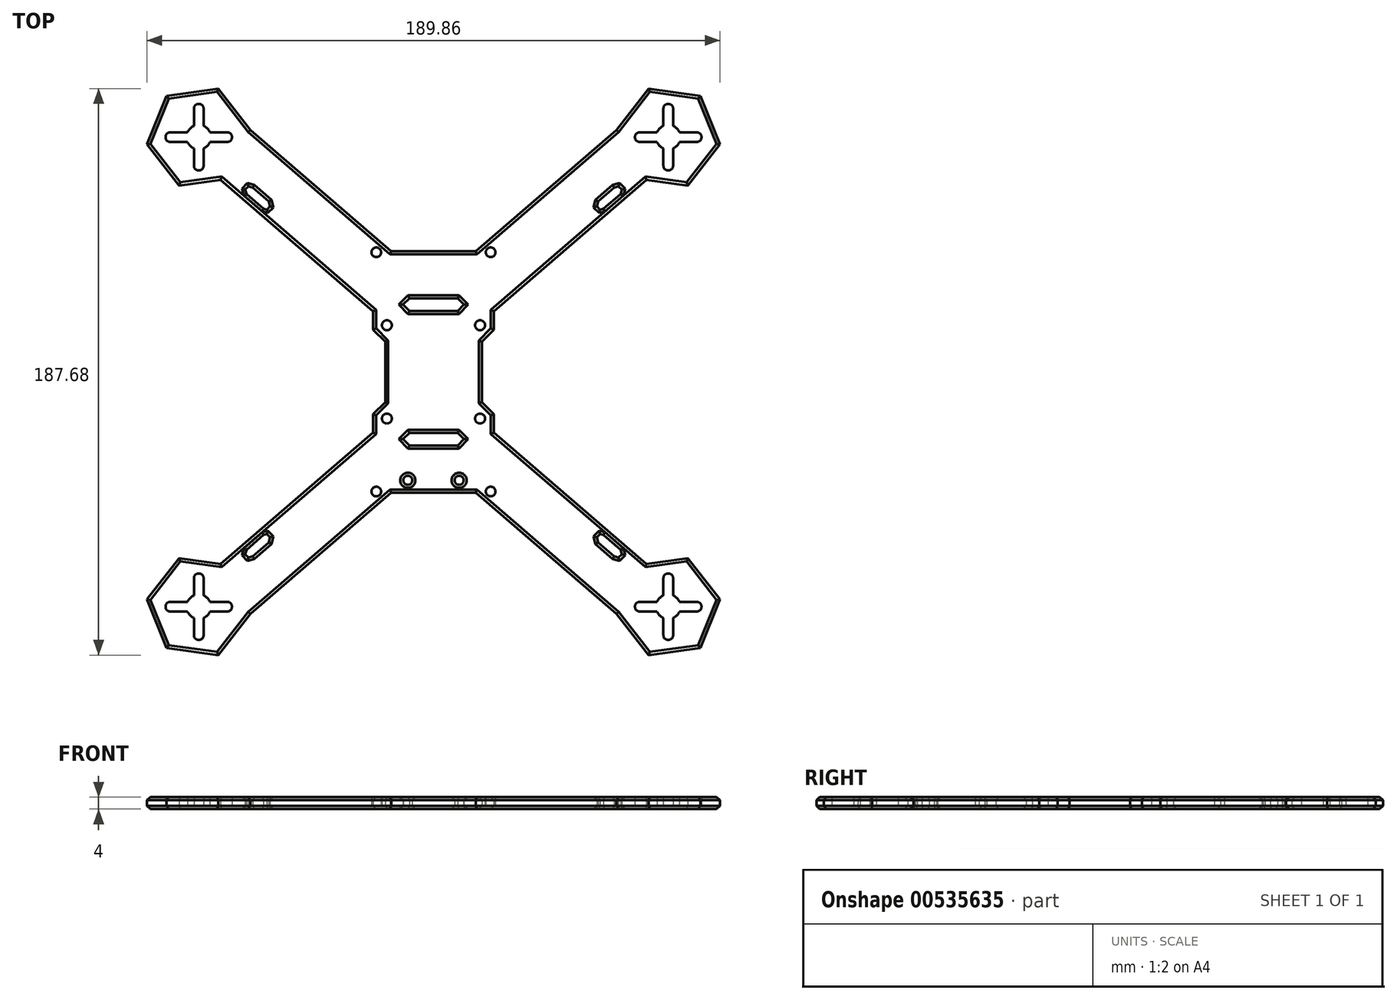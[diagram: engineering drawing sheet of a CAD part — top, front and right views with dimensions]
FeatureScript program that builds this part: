
annotation { "Feature Type Name" : "Feature", "Feature Type Description" : "" }
export const myFeature = defineFeature(function(context is Context, id is Id, definition is map)
    precondition{}
    {
        {
            var Q0;
            Q0=qCreatedBy(makeId("Top.planeOp"),FACE);
            var sketch = newSketch(context, id + "F0", { "sketchPlane" : qUnion([Q0])});
            skCircle(sketch, "E0", {"center": v(15.45, 15.45) * mm, "radius": 1.65 * mm});
            skPoint(sketch, "E1.middle", {"position": v(77.78, 77.78) * mm});
            skLineSegment(sketch, "E2.bottom", {"start": v(77.68, 66.78) * mm, "end": v(77.88, 66.78) * mm});
            skLineSegment(sketch, "E2.top", {"start": v(77.68, 88.78) * mm, "end": v(77.88, 88.78) * mm});
            skLineSegment(sketch, "E2.left", {"start": v(76.18, 68.28) * mm, "end": v(76.18, 76.29) * mm});
            skLineSegment(sketch, "E2.right", {"start": v(79.38, 68.28) * mm, "end": v(79.38, 76.18) * mm});
            skLineSegment(sketch, "E3.bottom", {"start": v(87.28, 79.38) * mm, "end": v(79.38, 79.38) * mm});
            skLineSegment(sketch, "E3.top", {"start": v(87.28, 76.18) * mm, "end": v(79.38, 76.18) * mm});
            skLineSegment(sketch, "E3.left", {"start": v(88.78, 77.88) * mm, "end": v(88.78, 77.68) * mm});
            skLineSegment(sketch, "E3.right", {"start": v(66.78, 77.88) * mm, "end": v(66.78, 77.68) * mm});
            skPoint(sketch, "E4.visualSharp", {"position": v(79.38, 88.78) * mm});
            skArc(sketch, "E4.filletArc", {"start": v(79.38, 87.28) * mm, "mid": v(78.94, 88.34) * mm, "end": v(77.88, 88.78) * mm});
            skPoint(sketch, "E5.visualSharp", {"position": v(76.18, 88.78) * mm});
            skArc(sketch, "E5.filletArc", {"start": v(77.68, 88.78) * mm, "mid": v(76.62, 88.34) * mm, "end": v(76.18, 87.28) * mm});
            skPoint(sketch, "E6.visualSharp", {"position": v(79.38, 66.78) * mm});
            skArc(sketch, "E6.filletArc", {"start": v(77.88, 66.78) * mm, "mid": v(78.94, 67.22) * mm, "end": v(79.38, 68.28) * mm});
            skPoint(sketch, "E7.visualSharp", {"position": v(76.18, 66.78) * mm});
            skArc(sketch, "E7.filletArc", {"start": v(76.18, 68.28) * mm, "mid": v(76.62, 67.22) * mm, "end": v(77.68, 66.78) * mm});
            skPoint(sketch, "E8.visualSharp", {"position": v(88.78, 79.38) * mm});
            skArc(sketch, "E8.filletArc", {"start": v(88.78, 77.88) * mm, "mid": v(88.34, 78.94) * mm, "end": v(87.28, 79.38) * mm});
            skPoint(sketch, "E9.visualSharp", {"position": v(88.78, 76.18) * mm});
            skArc(sketch, "E9.filletArc", {"start": v(87.28, 76.18) * mm, "mid": v(88.34, 76.62) * mm, "end": v(88.78, 77.68) * mm});
            skPoint(sketch, "E10.visualSharp", {"position": v(66.78, 79.38) * mm});
            skArc(sketch, "E10.filletArc", {"start": v(68.28, 79.38) * mm, "mid": v(67.22, 78.94) * mm, "end": v(66.78, 77.88) * mm});
            skPoint(sketch, "E11.visualSharp", {"position": v(66.78, 76.18) * mm});
            skArc(sketch, "E11.filletArc", {"start": v(66.78, 77.68) * mm, "mid": v(67.22, 76.62) * mm, "end": v(68.28, 76.18) * mm});
            skLineSegment(sketch, "E12.trimOffspring", {"start": v(76.18, 79.38) * mm, "end": v(76.18, 87.28) * mm});
            skLineSegment(sketch, "E13.trimOffspring", {"start": v(76.18, 76.18) * mm, "end": v(68.28, 76.18) * mm});
            skLineSegment(sketch, "E14.trimOffspring", {"start": v(76.18, 79.38) * mm, "end": v(68.28, 79.38) * mm});
            skLineSegment(sketch, "E15.trimOffspring", {"start": v(79.38, 79.38) * mm, "end": v(79.38, 87.28) * mm});
            skLineSegment(sketch, "E16.cCircle", {"start": v(49.17, 49.17) * mm, "end": v(49.17, 49.17) * mm});
            skLineSegment(sketch, "E17", {"start": v(77.78, 77.78) * mm, "end": v(0, 0) * mm, "construction": true});
            skLineSegment(sketch, "E18", {"start": v(60.63, 80.19) * mm, "end": v(14, 40) * mm});
            skLineSegment(sketch, "E19", {"start": v(20, 20.09) * mm, "end": v(70.54, 63.65) * mm});
            skLineSegment(sketch, "E20", {"start": v(20, 20.09) * mm, "end": v(20, 14) * mm});
            skLineSegment(sketch, "E21", {"start": v(14, 40) * mm, "end": v(0, 40) * mm});
            skLineSegment(sketch, "E22", {"start": v(61.99, 58.96) * mm, "end": v(56.29, 54.05) * mm});
            skCircle(sketch, "E23", {"center": v(77.78, 77.78) * mm, "radius": 63.5 * mm, "construction": true});
            skLineSegment(sketch, "E24", {"start": v(8, 20.17) * mm, "end": v(0, 20.17) * mm});
            skLineSegment(sketch, "E25", {"start": v(8, 20.17) * mm, "end": v(10.12, 22.3) * mm});
            skLineSegment(sketch, "E26", {"start": v(10.12, 22.3) * mm, "end": v(8, 24.41) * mm});
            skLineSegment(sketch, "E27", {"start": v(8, 24.41) * mm, "end": v(0, 24.41) * mm});
            skLineSegment(sketch, "E28", {"start": v(14, 40) * mm, "end": v(14, 0) * mm, "construction": true});
            skCircle(sketch, "E29", {"center": v(18.94, 39.63) * mm, "radius": 1.6 * mm});
            skLineSegment(sketch, "E30.3", {"start": v(59.86, 61.08) * mm, "end": v(61.31, 61.47) * mm});
            skLineSegment(sketch, "E30.4", {"start": v(61.31, 61.47) * mm, "end": v(62.37, 60.41) * mm});
            skLineSegment(sketch, "E30.5", {"start": v(62.37, 60.41) * mm, "end": v(61.99, 58.96) * mm});
            skLineSegment(sketch, "E31.0", {"start": v(56.29, 54.05) * mm, "end": v(55.18, 53.75) * mm});
            skLineSegment(sketch, "E31.1", {"start": v(55.18, 53.75) * mm, "end": v(54.12, 54.81) * mm});
            skLineSegment(sketch, "E31.2", {"start": v(54.12, 54.81) * mm, "end": v(54.56, 56.5) * mm});
            skLineSegment(sketch, "E32", {"start": v(14, 40) * mm, "end": v(21.57, 46.53) * mm, "construction": true});
            skLineSegment(sketch, "E33", {"start": v(21.57, 46.53) * mm, "end": v(26.14, 41.23) * mm, "construction": true});
            skLineSegment(sketch, "E34", {"start": v(26.14, 41.23) * mm, "end": v(18.57, 34.7) * mm, "construction": true});
            skLineSegment(sketch, "E35", {"start": v(18.57, 34.7) * mm, "end": v(14, 40) * mm, "construction": true});
            skLineSegment(sketch, "E36", {"start": v(59.86, 61.08) * mm, "end": v(54.56, 56.5) * mm});
            skArc(sketch, "E37.MirrorCS", {"start": v(-79.38, 87.28) * mm, "mid": v(-78.94, 88.34) * mm, "end": v(-77.88, 88.78) * mm});
            skArc(sketch, "E38.MirrorCS", {"start": v(-77.68, 88.78) * mm, "mid": v(-76.62, 88.34) * mm, "end": v(-76.18, 87.28) * mm});
            skLineSegment(sketch, "E39.MirrorCS", {"start": v(-76.18, 79.38) * mm, "end": v(-76.18, 87.28) * mm});
            skLineSegment(sketch, "E40.MirrorCS", {"start": v(-76.18, 68.28) * mm, "end": v(-76.18, 76.29) * mm});
            skLineSegment(sketch, "E41.MirrorCS", {"start": v(-79.38, 68.28) * mm, "end": v(-79.38, 76.18) * mm});
            skLineSegment(sketch, "E42.MirrorCS", {"start": v(-87.28, 79.38) * mm, "end": v(-79.38, 79.38) * mm});
            skLineSegment(sketch, "E43.MirrorCS", {"start": v(-87.28, 76.18) * mm, "end": v(-79.38, 76.18) * mm});
            skArc(sketch, "E44.MirrorCS", {"start": v(-77.88, 66.78) * mm, "mid": v(-78.94, 67.22) * mm, "end": v(-79.38, 68.28) * mm});
            skArc(sketch, "E45.MirrorCS", {"start": v(-76.18, 68.28) * mm, "mid": v(-76.62, 67.22) * mm, "end": v(-77.68, 66.78) * mm});
            skArc(sketch, "E46.MirrorCS", {"start": v(-88.78, 77.88) * mm, "mid": v(-88.34, 78.94) * mm, "end": v(-87.28, 79.38) * mm});
            skArc(sketch, "E47.MirrorCS", {"start": v(-87.28, 76.18) * mm, "mid": v(-88.34, 76.62) * mm, "end": v(-88.78, 77.68) * mm});
            skArc(sketch, "E48.MirrorCS", {"start": v(-68.28, 79.38) * mm, "mid": v(-67.22, 78.94) * mm, "end": v(-66.78, 77.88) * mm});
            skArc(sketch, "E49.MirrorCS", {"start": v(-66.78, 77.68) * mm, "mid": v(-67.22, 76.62) * mm, "end": v(-68.28, 76.18) * mm});
            skLineSegment(sketch, "E50.MirrorCS", {"start": v(-79.38, 79.38) * mm, "end": v(-79.38, 87.28) * mm});
            skLineSegment(sketch, "E51.MirrorCS", {"start": v(-10.12, 22.3) * mm, "end": v(-8, 24.41) * mm});
            skPoint(sketch, "E52.MirrorP", {"position": v(-77.78, 77.78) * mm});
            skLineSegment(sketch, "E53.MirrorCS", {"start": v(-8, 20.17) * mm, "end": v(-10.12, 22.3) * mm});
            skLineSegment(sketch, "E54.MirrorCS", {"start": v(-55.18, 53.75) * mm, "end": v(-54.12, 54.81) * mm});
            skLineSegment(sketch, "E55.MirrorCS", {"start": v(-54.12, 54.81) * mm, "end": v(-54.56, 56.5) * mm});
            skLineSegment(sketch, "E56.MirrorCS", {"start": v(-76.18, 76.18) * mm, "end": v(-68.28, 76.18) * mm});
            skLineSegment(sketch, "E57.MirrorCS", {"start": v(-76.18, 79.38) * mm, "end": v(-68.28, 79.38) * mm});
            skCircle(sketch, "E58.MirrorC", {"center": v(-15.45, 15.45) * mm, "radius": 1.65 * mm});
            skLineSegment(sketch, "E59.MirrorCS", {"start": v(-18.57, 34.7) * mm, "end": v(-14, 40) * mm, "construction": true});
            skCircle(sketch, "E60.MirrorC", {"center": v(-18.94, 39.63) * mm, "radius": 1.6 * mm});
            skLineSegment(sketch, "E61.MirrorCS", {"start": v(-62.37, 60.41) * mm, "end": v(-61.99, 58.96) * mm});
            skLineSegment(sketch, "E62.MirrorCS", {"start": v(-59.86, 61.08) * mm, "end": v(-54.56, 56.5) * mm});
            skLineSegment(sketch, "E63.MirrorCS", {"start": v(-59.86, 61.08) * mm, "end": v(-61.31, 61.47) * mm});
            skLineSegment(sketch, "E64.MirrorCS", {"start": v(-21.57, 46.53) * mm, "end": v(-26.14, 41.23) * mm, "construction": true});
            skLineSegment(sketch, "E65.MirrorCS", {"start": v(-56.29, 54.05) * mm, "end": v(-55.18, 53.75) * mm});
            skLineSegment(sketch, "E66.MirrorCS", {"start": v(-61.99, 58.96) * mm, "end": v(-56.29, 54.05) * mm});
            skLineSegment(sketch, "E67.MirrorCS", {"start": v(-61.31, 61.47) * mm, "end": v(-62.37, 60.41) * mm});
            skLineSegment(sketch, "E68.MirrorCS", {"start": v(-8, 24.41) * mm, "end": v(0, 24.41) * mm});
            skLineSegment(sketch, "E69.MirrorCS", {"start": v(-14, 40) * mm, "end": v(-21.57, 46.53) * mm, "construction": true});
            skLineSegment(sketch, "E70.MirrorCS", {"start": v(-20, 20.09) * mm, "end": v(-70.54, 63.65) * mm});
            skPoint(sketch, "E71.MirrorP", {"position": v(-79.38, 88.78) * mm});
            skPoint(sketch, "E72.MirrorP", {"position": v(-88.78, 76.18) * mm});
            skCircle(sketch, "E73.MirrorC", {"center": v(-77.78, 77.78) * mm, "radius": 63.5 * mm, "construction": true});
            skPoint(sketch, "E74.MirrorP", {"position": v(-76.18, 66.78) * mm});
            skPoint(sketch, "E75.MirrorP", {"position": v(-79.38, 66.78) * mm});
            skLineSegment(sketch, "E76.MirrorCS", {"start": v(-14, 40) * mm, "end": v(-14, 0) * mm, "construction": true});
            skLineSegment(sketch, "E77.MirrorCS", {"start": v(-8, 20.17) * mm, "end": v(0, 20.17) * mm});
            skLineSegment(sketch, "E78.MirrorCS", {"start": v(-14, 40) * mm, "end": v(0, 40) * mm});
            skPoint(sketch, "E79.MirrorP", {"position": v(-76.18, 88.78) * mm});
            skLineSegment(sketch, "E80.MirrorCS", {"start": v(-26.14, 41.23) * mm, "end": v(-18.57, 34.7) * mm, "construction": true});
            skLineSegment(sketch, "E81.MirrorCS", {"start": v(-77.78, 77.78) * mm, "end": v(0, 0) * mm, "construction": true});
            skPoint(sketch, "E82.MirrorP", {"position": v(-66.78, 76.18) * mm});
            skPoint(sketch, "E83.MirrorP", {"position": v(-66.78, 79.38) * mm});
            skPoint(sketch, "E84.MirrorP", {"position": v(-88.78, 79.38) * mm});
            skLineSegment(sketch, "E85.MirrorCS", {"start": v(-60.63, 80.19) * mm, "end": v(-14, 40) * mm});
            skArc(sketch, "E86.MirrorCS", {"start": v(76.18, -68.28) * mm, "mid": v(76.62, -67.22) * mm, "end": v(77.68, -66.78) * mm});
            skArc(sketch, "E87.MirrorCS", {"start": v(77.88, -66.78) * mm, "mid": v(78.94, -67.22) * mm, "end": v(79.38, -68.28) * mm});
            skArc(sketch, "E88.MirrorCS", {"start": v(77.68, -88.78) * mm, "mid": v(76.62, -88.34) * mm, "end": v(76.18, -87.28) * mm});
            skArc(sketch, "E89.MirrorCS", {"start": v(79.38, -87.28) * mm, "mid": v(78.94, -88.34) * mm, "end": v(77.88, -88.78) * mm});
            skLineSegment(sketch, "E90.MirrorCS", {"start": v(76.18, -79.38) * mm, "end": v(76.18, -87.28) * mm});
            skLineSegment(sketch, "E91.MirrorCS", {"start": v(-76.18, -79.38) * mm, "end": v(-76.18, -87.28) * mm});
            skArc(sketch, "E92.MirrorCS", {"start": v(-77.68, -88.78) * mm, "mid": v(-76.62, -88.34) * mm, "end": v(-76.18, -87.28) * mm});
            skLineSegment(sketch, "E93.MirrorCS", {"start": v(79.38, -79.38) * mm, "end": v(79.38, -87.28) * mm});
            skArc(sketch, "E94.MirrorCS", {"start": v(66.78, -77.68) * mm, "mid": v(67.22, -76.62) * mm, "end": v(68.28, -76.18) * mm});
            skArc(sketch, "E95.MirrorCS", {"start": v(68.28, -79.38) * mm, "mid": v(67.22, -78.94) * mm, "end": v(66.78, -77.88) * mm});
            skArc(sketch, "E96.MirrorCS", {"start": v(87.28, -76.18) * mm, "mid": v(88.34, -76.62) * mm, "end": v(88.78, -77.68) * mm});
            skArc(sketch, "E97.MirrorCS", {"start": v(88.78, -77.88) * mm, "mid": v(88.34, -78.94) * mm, "end": v(87.28, -79.38) * mm});
            skLineSegment(sketch, "E98.MirrorCS", {"start": v(87.28, -76.18) * mm, "end": v(79.38, -76.18) * mm});
            skLineSegment(sketch, "E99.MirrorCS", {"start": v(79.38, -68.28) * mm, "end": v(79.38, -76.18) * mm});
            skLineSegment(sketch, "E100.MirrorCS", {"start": v(76.18, -68.28) * mm, "end": v(76.18, -76.29) * mm});
            skLineSegment(sketch, "E101.MirrorCS", {"start": v(76.18, -79.38) * mm, "end": v(68.28, -79.38) * mm});
            skLineSegment(sketch, "E102.MirrorCS", {"start": v(76.18, -76.18) * mm, "end": v(68.28, -76.18) * mm});
            skArc(sketch, "E103.MirrorCS", {"start": v(-79.38, -87.28) * mm, "mid": v(-78.94, -88.34) * mm, "end": v(-77.88, -88.78) * mm});
            skLineSegment(sketch, "E104.MirrorCS", {"start": v(-79.38, -79.38) * mm, "end": v(-79.38, -87.28) * mm});
            skArc(sketch, "E105.MirrorCS", {"start": v(-87.28, -76.18) * mm, "mid": v(-88.34, -76.62) * mm, "end": v(-88.78, -77.68) * mm});
            skArc(sketch, "E106.MirrorCS", {"start": v(-88.78, -77.88) * mm, "mid": v(-88.34, -78.94) * mm, "end": v(-87.28, -79.38) * mm});
            skArc(sketch, "E107.MirrorCS", {"start": v(-76.18, -68.28) * mm, "mid": v(-76.62, -67.22) * mm, "end": v(-77.68, -66.78) * mm});
            skLineSegment(sketch, "E108.MirrorCS", {"start": v(87.28, -79.38) * mm, "end": v(79.38, -79.38) * mm});
            skArc(sketch, "E109.MirrorCS", {"start": v(-77.88, -66.78) * mm, "mid": v(-78.94, -67.22) * mm, "end": v(-79.38, -68.28) * mm});
            skLineSegment(sketch, "E110.MirrorCS", {"start": v(-87.28, -79.38) * mm, "end": v(-79.38, -79.38) * mm});
            skArc(sketch, "E111.MirrorCS", {"start": v(-66.78, -77.68) * mm, "mid": v(-67.22, -76.62) * mm, "end": v(-68.28, -76.18) * mm});
            skPoint(sketch, "E112.MirrorP", {"position": v(77.78, -77.78) * mm});
            skLineSegment(sketch, "E113.MirrorCS", {"start": v(-87.28, -76.18) * mm, "end": v(-79.38, -76.18) * mm});
            skLineSegment(sketch, "E114.MirrorCS", {"start": v(54.12, -54.81) * mm, "end": v(54.56, -56.5) * mm});
            skArc(sketch, "E115.MirrorCS", {"start": v(-68.28, -79.38) * mm, "mid": v(-67.22, -78.94) * mm, "end": v(-66.78, -77.88) * mm});
            skLineSegment(sketch, "E116.MirrorCS", {"start": v(55.18, -53.75) * mm, "end": v(54.12, -54.81) * mm});
            skLineSegment(sketch, "E117.MirrorCS", {"start": v(-76.18, -68.28) * mm, "end": v(-76.18, -76.29) * mm});
            skLineSegment(sketch, "E118.MirrorCS", {"start": v(-59.86, -61.08) * mm, "end": v(-61.31, -61.47) * mm});
            skLineSegment(sketch, "E119.MirrorCS", {"start": v(8, -20.17) * mm, "end": v(10.12, -22.3) * mm});
            skLineSegment(sketch, "E120.MirrorCS", {"start": v(56.29, -54.05) * mm, "end": v(55.18, -53.75) * mm});
            skLineSegment(sketch, "E121.MirrorCS", {"start": v(59.86, -61.08) * mm, "end": v(54.56, -56.5) * mm});
            skLineSegment(sketch, "E122.MirrorCS", {"start": v(62.37, -60.41) * mm, "end": v(61.99, -58.96) * mm});
            skLineSegment(sketch, "E123.MirrorCS", {"start": v(-54.12, -54.81) * mm, "end": v(-54.56, -56.5) * mm});
            skLineSegment(sketch, "E124.MirrorCS", {"start": v(-59.86, -61.08) * mm, "end": v(-54.56, -56.5) * mm});
            skLineSegment(sketch, "E125.MirrorCS", {"start": v(18.57, -34.7) * mm, "end": v(14, -40) * mm, "construction": true});
            skCircle(sketch, "E126.MirrorC", {"center": v(15.45, -15.45) * mm, "radius": 1.65 * mm});
            skLineSegment(sketch, "E127.MirrorCS", {"start": v(61.31, -61.47) * mm, "end": v(62.37, -60.41) * mm});
            skLineSegment(sketch, "E128.MirrorCS", {"start": v(-62.37, -60.41) * mm, "end": v(-61.99, -58.96) * mm});
            skLineSegment(sketch, "E129.MirrorCS", {"start": v(-55.18, -53.75) * mm, "end": v(-54.12, -54.81) * mm});
            skLineSegment(sketch, "E130.MirrorCS", {"start": v(61.99, -58.96) * mm, "end": v(56.29, -54.05) * mm});
            skLineSegment(sketch, "E131.MirrorCS", {"start": v(-10.12, -22.3) * mm, "end": v(-8, -24.41) * mm});
            skLineSegment(sketch, "E132.MirrorCS", {"start": v(-18.57, -34.7) * mm, "end": v(-14, -40) * mm, "construction": true});
            skLineSegment(sketch, "E133.MirrorCS", {"start": v(-61.31, -61.47) * mm, "end": v(-62.37, -60.41) * mm});
            skLineSegment(sketch, "E134.MirrorCS", {"start": v(-56.29, -54.05) * mm, "end": v(-55.18, -53.75) * mm});
            skLineSegment(sketch, "E135.MirrorCS", {"start": v(21.57, -46.53) * mm, "end": v(26.14, -41.23) * mm, "construction": true});
            skLineSegment(sketch, "E136.MirrorCS", {"start": v(59.86, -61.08) * mm, "end": v(61.31, -61.47) * mm});
            skLineSegment(sketch, "E137.MirrorCS", {"start": v(-8, -20.17) * mm, "end": v(-10.12, -22.3) * mm});
            skLineSegment(sketch, "E138.MirrorCS", {"start": v(-61.99, -58.96) * mm, "end": v(-56.29, -54.05) * mm});
            skLineSegment(sketch, "E139.MirrorCS", {"start": v(-79.38, -68.28) * mm, "end": v(-79.38, -76.18) * mm});
            skLineSegment(sketch, "E140.MirrorCS", {"start": v(-21.57, -46.53) * mm, "end": v(-26.14, -41.23) * mm, "construction": true});
            skLineSegment(sketch, "E141.MirrorCS", {"start": v(10.12, -22.3) * mm, "end": v(8, -24.41) * mm});
            skPoint(sketch, "E142.MirrorP", {"position": v(-77.78, -77.78) * mm});
            skLineSegment(sketch, "E143.MirrorCS", {"start": v(26.14, -41.23) * mm, "end": v(18.57, -34.7) * mm, "construction": true});
            skCircle(sketch, "E144.MirrorC", {"center": v(18.94, -39.63) * mm, "radius": 1.6 * mm});
            skLineSegment(sketch, "E145.MirrorCS", {"start": v(14, -40) * mm, "end": v(21.57, -46.53) * mm, "construction": true});
            skLineSegment(sketch, "E146.MirrorCS", {"start": v(8, -24.41) * mm, "end": v(0, -24.41) * mm});
            skCircle(sketch, "E147.MirrorC", {"center": v(-18.94, -39.63) * mm, "radius": 1.6 * mm});
            skLineSegment(sketch, "E148.MirrorCS", {"start": v(14, -40) * mm, "end": v(0, -40) * mm});
            skCircle(sketch, "E149.MirrorC", {"center": v(-15.45, -15.45) * mm, "radius": 1.65 * mm});
            skLineSegment(sketch, "E150.MirrorCS", {"start": v(-26.14, -41.23) * mm, "end": v(-18.57, -34.7) * mm, "construction": true});
            skPoint(sketch, "E151.MirrorP", {"position": v(-76.18, -88.78) * mm});
            skLineSegment(sketch, "E152.MirrorCS", {"start": v(-76.18, -79.38) * mm, "end": v(-68.28, -79.38) * mm});
            skLineSegment(sketch, "E153.MirrorCS", {"start": v(-20, -20.09) * mm, "end": v(-70.54, -63.65) * mm});
            skLineSegment(sketch, "E154.MirrorCS", {"start": v(60.63, -80.19) * mm, "end": v(14, -40) * mm});
            skLineSegment(sketch, "E155.MirrorCS", {"start": v(-14, -40) * mm, "end": v(0, -40) * mm});
            skPoint(sketch, "E156.MirrorP", {"position": v(76.18, -88.78) * mm});
            skLineSegment(sketch, "E157.MirrorCS", {"start": v(-76.18, -76.18) * mm, "end": v(-68.28, -76.18) * mm});
            skLineSegment(sketch, "E158.MirrorCS", {"start": v(77.78, -77.78) * mm, "end": v(0, 0) * mm, "construction": true});
            skLineSegment(sketch, "E159.MirrorCS", {"start": v(-8, -20.17) * mm, "end": v(0, -20.17) * mm});
            skLineSegment(sketch, "E160.MirrorCS", {"start": v(8, -20.17) * mm, "end": v(0, -20.17) * mm});
            skPoint(sketch, "E161.MirrorP", {"position": v(88.78, -79.38) * mm});
            skPoint(sketch, "E162.MirrorP", {"position": v(-79.38, -66.78) * mm});
            skLineSegment(sketch, "E163.MirrorCS", {"start": v(-14, -40) * mm, "end": v(-21.57, -46.53) * mm, "construction": true});
            skPoint(sketch, "E164.MirrorP", {"position": v(79.38, -88.78) * mm});
            skLineSegment(sketch, "E165.MirrorCS", {"start": v(-14, -40) * mm, "end": v(-14, 0) * mm, "construction": true});
            skCircle(sketch, "E166.MirrorC", {"center": v(77.78, -77.78) * mm, "radius": 63.5 * mm, "construction": true});
            skPoint(sketch, "E167.MirrorP", {"position": v(-76.18, -66.78) * mm});
            skLineSegment(sketch, "E168.MirrorCS", {"start": v(-8, -24.41) * mm, "end": v(0, -24.41) * mm});
            skPoint(sketch, "E169.MirrorP", {"position": v(76.18, -66.78) * mm});
            skPoint(sketch, "E170.MirrorP", {"position": v(66.78, -79.38) * mm});
            skPoint(sketch, "E171.MirrorP", {"position": v(-66.78, -79.38) * mm});
            skCircle(sketch, "E172.MirrorC", {"center": v(-77.78, -77.78) * mm, "radius": 63.5 * mm, "construction": true});
            skLineSegment(sketch, "E173.MirrorCS", {"start": v(20, -20.09) * mm, "end": v(20, -14) * mm});
            skLineSegment(sketch, "E174.MirrorCS", {"start": v(14, -40) * mm, "end": v(14, 0) * mm, "construction": true});
            skLineSegment(sketch, "E175.MirrorCS", {"start": v(-77.78, -77.78) * mm, "end": v(0, 0) * mm, "construction": true});
            skPoint(sketch, "E176.MirrorP", {"position": v(-79.38, -88.78) * mm});
            skPoint(sketch, "E177.MirrorP", {"position": v(-88.78, -79.38) * mm});
            skPoint(sketch, "E178.MirrorP", {"position": v(79.38, -66.78) * mm});
            skPoint(sketch, "E179.MirrorP", {"position": v(88.78, -76.18) * mm});
            skPoint(sketch, "E180.MirrorP", {"position": v(-66.78, -76.18) * mm});
            skPoint(sketch, "E181.MirrorP", {"position": v(-88.78, -76.18) * mm});
            skPoint(sketch, "E182.MirrorP", {"position": v(66.78, -76.18) * mm});
            skLineSegment(sketch, "E183.MirrorCS", {"start": v(20, -20.09) * mm, "end": v(70.54, -63.65) * mm});
            skLineSegment(sketch, "E184.MirrorCS", {"start": v(-60.63, -80.19) * mm, "end": v(-14, -40) * mm});
            skCircle(sketch, "E185", {"center": v(8.5, -35.92) * mm, "radius": 1.5 * mm});
            skCircle(sketch, "E186.MirrorC", {"center": v(-8.5, -35.92) * mm, "radius": 1.5 * mm});
            skLineSegment(sketch, "E187", {"start": v(20, -14) * mm, "end": v(16, -10) * mm});
            skLineSegment(sketch, "E188", {"start": v(16, -10) * mm, "end": v(16, 0) * mm});
            skLineSegment(sketch, "E189.MirrorCS", {"start": v(20, 14) * mm, "end": v(16, 10) * mm});
            skLineSegment(sketch, "E190.MirrorCS", {"start": v(16, 10) * mm, "end": v(16, 0) * mm});
            skLineSegment(sketch, "E191.MirrorCS", {"start": v(-20, 20.09) * mm, "end": v(-20, 14) * mm});
            skLineSegment(sketch, "E192.MirrorCS", {"start": v(-16, 10) * mm, "end": v(-16, 0) * mm});
            skLineSegment(sketch, "E193.MirrorCS", {"start": v(-20, -20.09) * mm, "end": v(-20, -14) * mm});
            skLineSegment(sketch, "E194.MirrorCS", {"start": v(-20, -14) * mm, "end": v(-16, -10) * mm});
            skLineSegment(sketch, "E195.MirrorCS", {"start": v(-16, -10) * mm, "end": v(-16, 0) * mm});
            skLineSegment(sketch, "E196.MirrorCS", {"start": v(-20, 14) * mm, "end": v(-16, 10) * mm});
            skLineSegment(sketch, "E197.0", {"start": v(71.29, -93.84) * mm, "end": v(60.63, -80.19) * mm});
            skLineSegment(sketch, "E197.2", {"start": v(70.54, -63.65) * mm, "end": v(84.28, -61.72) * mm});
            skLineSegment(sketch, "E197.3", {"start": v(84.28, -61.72) * mm, "end": v(94.93, -75.38) * mm});
            skLineSegment(sketch, "E197.4", {"start": v(94.93, -75.38) * mm, "end": v(88.44, -91.43) * mm});
            skLineSegment(sketch, "E197.5", {"start": v(88.44, -91.43) * mm, "end": v(71.29, -93.84) * mm});
            skPoint(sketch, "E197.0.midPoint", {"position": v(65.96, -87.01) * mm});
            skLineSegment(sketch, "E198.MirrorCS", {"start": v(-70.54, -63.65) * mm, "end": v(-84.28, -61.72) * mm});
            skLineSegment(sketch, "E199.MirrorCS", {"start": v(-84.28, -61.72) * mm, "end": v(-94.93, -75.38) * mm});
            skLineSegment(sketch, "E200.MirrorCS", {"start": v(-94.93, -75.38) * mm, "end": v(-88.44, -91.43) * mm});
            skLineSegment(sketch, "E201.MirrorCS", {"start": v(-71.29, -93.84) * mm, "end": v(-60.63, -80.19) * mm});
            skLineSegment(sketch, "E202.MirrorCS", {"start": v(-88.44, -91.43) * mm, "end": v(-71.29, -93.84) * mm});
            skLineSegment(sketch, "E203.MirrorCS", {"start": v(-70.54, 63.65) * mm, "end": v(-84.28, 61.72) * mm});
            skLineSegment(sketch, "E204.MirrorCS", {"start": v(-84.28, 61.72) * mm, "end": v(-94.93, 75.38) * mm});
            skLineSegment(sketch, "E205.MirrorCS", {"start": v(-94.93, 75.38) * mm, "end": v(-88.44, 91.43) * mm});
            skLineSegment(sketch, "E206.MirrorCS", {"start": v(-71.29, 93.84) * mm, "end": v(-60.63, 80.19) * mm});
            skLineSegment(sketch, "E207.MirrorCS", {"start": v(-88.44, 91.43) * mm, "end": v(-71.29, 93.84) * mm});
            skLineSegment(sketch, "E208.MirrorCS", {"start": v(70.54, 63.65) * mm, "end": v(84.28, 61.72) * mm});
            skLineSegment(sketch, "E209.MirrorCS", {"start": v(84.28, 61.72) * mm, "end": v(94.93, 75.38) * mm});
            skLineSegment(sketch, "E210.MirrorCS", {"start": v(94.93, 75.38) * mm, "end": v(88.44, 91.43) * mm});
            skLineSegment(sketch, "E211.MirrorCS", {"start": v(71.29, 93.84) * mm, "end": v(60.63, 80.19) * mm});
            skLineSegment(sketch, "E212.MirrorCS", {"start": v(88.44, 91.43) * mm, "end": v(71.29, 93.84) * mm});
            skLineSegment(sketch, "E213", {"start": v(-77.68, -66.78) * mm, "end": v(-77.88, -66.78) * mm});
            skLineSegment(sketch, "E214", {"start": v(-77.68, -88.78) * mm, "end": v(-77.88, -88.78) * mm});
            skLineSegment(sketch, "E215", {"start": v(-88.78, -77.68) * mm, "end": v(-88.78, -77.88) * mm});
            skLineSegment(sketch, "E216", {"start": v(-66.78, -77.68) * mm, "end": v(-66.78, -77.88) * mm});
            skLineSegment(sketch, "E217", {"start": v(-77.68, 88.78) * mm, "end": v(-77.88, 88.78) * mm});
            skLineSegment(sketch, "E218", {"start": v(-66.78, 77.88) * mm, "end": v(-66.78, 77.68) * mm});
            skLineSegment(sketch, "E219", {"start": v(-88.78, 77.88) * mm, "end": v(-88.78, 77.68) * mm});
            skLineSegment(sketch, "E220", {"start": v(-77.88, 66.78) * mm, "end": v(-77.68, 66.78) * mm});
            skLineSegment(sketch, "E221", {"start": v(88.78, -77.68) * mm, "end": v(88.78, -77.88) * mm});
            skLineSegment(sketch, "E222", {"start": v(77.68, -66.78) * mm, "end": v(77.88, -66.78) * mm});
            skLineSegment(sketch, "E223", {"start": v(66.78, -77.68) * mm, "end": v(66.78, -77.88) * mm});
            skLineSegment(sketch, "E224", {"start": v(77.68, -88.78) * mm, "end": v(77.88, -88.78) * mm});
            skCircle(sketch, "E225", {"center": v(77.78, 77.78) * mm, "radius": 4.05 * mm});
            skCircle(sketch, "E226.MirrorC", {"center": v(-77.78, 77.78) * mm, "radius": 4.05 * mm});
            skCircle(sketch, "E227.MirrorC", {"center": v(77.78, -77.78) * mm, "radius": 4.05 * mm});
            skCircle(sketch, "E228.MirrorC", {"center": v(-77.78, -77.78) * mm, "radius": 4.05 * mm});
            skSolve(sketch);
        }
        {
            var Q0;
            Q0=makeQuery(id+"F0.imprint","IMPRINT",FACE,{"disambiguationData":[TD([[makeQuery(id+"F0.imprint","IMPRINT",EDGE,{"derivedFrom":sQuery(id+"F0.wireOp",EDGE,"E0")}),-1.0]])]});
            extrude(context, id + "F1", {"entities" : qUnion([Q0]), "depth" : 4 * mm});
        }
        {
            var Q0;
            Q0=makeQuery(id+"F1.opExtrude","CAP_EDGE",EDGE,{"disambiguationData":[OSD([sQuery(id+"F0.wireOp",EDGE,"E119.MirrorCS")])],"isStart":true});
            var Q1;
            Q1=makeQuery(id+"F1.opExtrude","CAP_EDGE",EDGE,{"disambiguationData":[OSD([sQuery(id+"F0.wireOp",EDGE,"E141.MirrorCS")])],"isStart":true});
            var Q2;
            Q2=makeQuery(id+"F1.opExtrude","CAP_EDGE",EDGE,{"disambiguationData":[OSD([sQuery(id+"F0.wireOp",EDGE,"E159.MirrorCS"),sQuery(id+"F0.wireOp",EDGE,"E160.MirrorCS")])],"isStart":true});
            var Q3;
            Q3=makeQuery(id+"F1.opExtrude","CAP_EDGE",EDGE,{"disambiguationData":[OSD([sQuery(id+"F0.wireOp",EDGE,"E137.MirrorCS")])],"isStart":true});
            var Q4;
            Q4=makeQuery(id+"F1.opExtrude","CAP_EDGE",EDGE,{"disambiguationData":[OSD([sQuery(id+"F0.wireOp",EDGE,"E131.MirrorCS")])],"isStart":true});
            var Q5;
            Q5=makeQuery(id+"F1.opExtrude","CAP_EDGE",EDGE,{"disambiguationData":[OSD([sQuery(id+"F0.wireOp",EDGE,"E146.MirrorCS"),sQuery(id+"F0.wireOp",EDGE,"E168.MirrorCS")])],"isStart":true});
            var Q6;
            Q6=makeQuery(id+"F1.opExtrude","CAP_EDGE",EDGE,{"disambiguationData":[OSD([sQuery(id+"F0.wireOp",EDGE,"E27"),sQuery(id+"F0.wireOp",EDGE,"E68.MirrorCS")])],"isStart":true});
            var Q7;
            Q7=makeQuery(id+"F1.opExtrude","CAP_EDGE",EDGE,{"disambiguationData":[OSD([sQuery(id+"F0.wireOp",EDGE,"E26")])],"isStart":true});
            var Q8;
            Q8=makeQuery(id+"F1.opExtrude","CAP_EDGE",EDGE,{"disambiguationData":[OSD([sQuery(id+"F0.wireOp",EDGE,"E25")])],"isStart":true});
            var Q9;
            Q9=makeQuery(id+"F1.opExtrude","CAP_EDGE",EDGE,{"disambiguationData":[OSD([sQuery(id+"F0.wireOp",EDGE,"E24"),sQuery(id+"F0.wireOp",EDGE,"E77.MirrorCS")])],"isStart":true});
            var Q10;
            Q10=makeQuery(id+"F1.opExtrude","CAP_EDGE",EDGE,{"disambiguationData":[OSD([sQuery(id+"F0.wireOp",EDGE,"E53.MirrorCS")])],"isStart":true});
            var Q11;
            Q11=makeQuery(id+"F1.opExtrude","CAP_EDGE",EDGE,{"disambiguationData":[OSD([sQuery(id+"F0.wireOp",EDGE,"E51.MirrorCS")])],"isStart":true});
            chamfer(context, id + "F2", {"entities" : qUnion([Q0, Q1, Q2, Q3, Q4, Q5, Q6, Q7, Q8, Q9, Q10, Q11]), "width" : 1 * mm, "tangentPropagation" : true});
        }
        {
            var Q0;
            Q0=makeQuery(id+"F1.opExtrude","CAP_EDGE",EDGE,{"disambiguationData":[OSD([sQuery(id+"F0.wireOp",EDGE,"E51.MirrorCS")])],"isStart":false});
            var Q1;
            Q1=makeQuery(id+"F1.opExtrude","CAP_EDGE",EDGE,{"disambiguationData":[OSD([sQuery(id+"F0.wireOp",EDGE,"E53.MirrorCS")])],"isStart":false});
            var Q2;
            Q2=makeQuery(id+"F1.opExtrude","CAP_EDGE",EDGE,{"disambiguationData":[OSD([sQuery(id+"F0.wireOp",EDGE,"E24"),sQuery(id+"F0.wireOp",EDGE,"E77.MirrorCS")])],"isStart":false});
            var Q3;
            Q3=makeQuery(id+"F1.opExtrude","CAP_EDGE",EDGE,{"disambiguationData":[OSD([sQuery(id+"F0.wireOp",EDGE,"E27"),sQuery(id+"F0.wireOp",EDGE,"E68.MirrorCS")])],"isStart":false});
            var Q4;
            Q4=makeQuery(id+"F1.opExtrude","CAP_EDGE",EDGE,{"disambiguationData":[OSD([sQuery(id+"F0.wireOp",EDGE,"E26")])],"isStart":false});
            var Q5;
            Q5=makeQuery(id+"F1.opExtrude","CAP_EDGE",EDGE,{"disambiguationData":[OSD([sQuery(id+"F0.wireOp",EDGE,"E25")])],"isStart":false});
            var Q6;
            Q6=makeQuery(id+"F1.opExtrude","CAP_EDGE",EDGE,{"disambiguationData":[OSD([sQuery(id+"F0.wireOp",EDGE,"E137.MirrorCS")])],"isStart":false});
            var Q7;
            Q7=makeQuery(id+"F1.opExtrude","CAP_EDGE",EDGE,{"disambiguationData":[OSD([sQuery(id+"F0.wireOp",EDGE,"E131.MirrorCS")])],"isStart":false});
            var Q8;
            Q8=makeQuery(id+"F1.opExtrude","CAP_EDGE",EDGE,{"disambiguationData":[OSD([sQuery(id+"F0.wireOp",EDGE,"E159.MirrorCS"),sQuery(id+"F0.wireOp",EDGE,"E160.MirrorCS")])],"isStart":false});
            var Q9;
            Q9=makeQuery(id+"F1.opExtrude","CAP_EDGE",EDGE,{"disambiguationData":[OSD([sQuery(id+"F0.wireOp",EDGE,"E146.MirrorCS"),sQuery(id+"F0.wireOp",EDGE,"E168.MirrorCS")])],"isStart":false});
            var Q10;
            Q10=makeQuery(id+"F1.opExtrude","CAP_EDGE",EDGE,{"disambiguationData":[OSD([sQuery(id+"F0.wireOp",EDGE,"E141.MirrorCS")])],"isStart":false});
            var Q11;
            Q11=makeQuery(id+"F1.opExtrude","CAP_EDGE",EDGE,{"disambiguationData":[OSD([sQuery(id+"F0.wireOp",EDGE,"E119.MirrorCS")])],"isStart":false});
            chamfer(context, id + "F3", {"entities" : qUnion([Q0, Q1, Q2, Q3, Q4, Q5, Q6, Q7, Q8, Q9, Q10, Q11]), "width" : 1 * mm, "tangentPropagation" : true});
        }
        {
            var Q0;
            Q0=makeQuery(id+"F1.opExtrude","CAP_EDGE",EDGE,{"disambiguationData":[OSD([sQuery(id+"F0.wireOp",EDGE,"E36")])],"isStart":false});
            var Q1;
            Q1=makeQuery(id+"F1.opExtrude","CAP_EDGE",EDGE,{"disambiguationData":[OSD([sQuery(id+"F0.wireOp",EDGE,"E30.3")])],"isStart":false});
            var Q2;
            Q2=makeQuery(id+"F1.opExtrude","CAP_EDGE",EDGE,{"disambiguationData":[OSD([sQuery(id+"F0.wireOp",EDGE,"E30.4")])],"isStart":false});
            var Q3;
            Q3=makeQuery(id+"F1.opExtrude","CAP_EDGE",EDGE,{"disambiguationData":[OSD([sQuery(id+"F0.wireOp",EDGE,"E30.5")])],"isStart":false});
            var Q4;
            Q4=makeQuery(id+"F1.opExtrude","CAP_EDGE",EDGE,{"disambiguationData":[OSD([sQuery(id+"F0.wireOp",EDGE,"E22")])],"isStart":false});
            var Q5;
            Q5=makeQuery(id+"F1.opExtrude","CAP_EDGE",EDGE,{"disambiguationData":[OSD([sQuery(id+"F0.wireOp",EDGE,"E31.0")])],"isStart":false});
            var Q6;
            Q6=makeQuery(id+"F1.opExtrude","CAP_EDGE",EDGE,{"disambiguationData":[OSD([sQuery(id+"F0.wireOp",EDGE,"E31.1")])],"isStart":false});
            var Q7;
            Q7=makeQuery(id+"F1.opExtrude","CAP_EDGE",EDGE,{"disambiguationData":[OSD([sQuery(id+"F0.wireOp",EDGE,"E31.2")])],"isStart":false});
            var Q8;
            Q8=makeQuery(id+"F1.opExtrude","CAP_EDGE",EDGE,{"disambiguationData":[OSD([sQuery(id+"F0.wireOp",EDGE,"E22")])],"isStart":true});
            var Q9;
            Q9=makeQuery(id+"F1.opExtrude","CAP_EDGE",EDGE,{"disambiguationData":[OSD([sQuery(id+"F0.wireOp",EDGE,"E31.0")])],"isStart":true});
            var Q10;
            Q10=makeQuery(id+"F1.opExtrude","CAP_EDGE",EDGE,{"disambiguationData":[OSD([sQuery(id+"F0.wireOp",EDGE,"E31.1")])],"isStart":true});
            var Q11;
            Q11=makeQuery(id+"F1.opExtrude","CAP_EDGE",EDGE,{"disambiguationData":[OSD([sQuery(id+"F0.wireOp",EDGE,"E31.2")])],"isStart":true});
            var Q12;
            Q12=makeQuery(id+"F1.opExtrude","CAP_EDGE",EDGE,{"disambiguationData":[OSD([sQuery(id+"F0.wireOp",EDGE,"E36")])],"isStart":true});
            var Q13;
            Q13=makeQuery(id+"F1.opExtrude","CAP_EDGE",EDGE,{"disambiguationData":[OSD([sQuery(id+"F0.wireOp",EDGE,"E30.3")])],"isStart":true});
            var Q14;
            Q14=makeQuery(id+"F1.opExtrude","CAP_EDGE",EDGE,{"disambiguationData":[OSD([sQuery(id+"F0.wireOp",EDGE,"E30.4")])],"isStart":true});
            var Q15;
            Q15=makeQuery(id+"F1.opExtrude","CAP_EDGE",EDGE,{"disambiguationData":[OSD([sQuery(id+"F0.wireOp",EDGE,"E30.5")])],"isStart":true});
            chamfer(context, id + "F4", {"entities" : qUnion([Q0, Q1, Q2, Q3, Q4, Q5, Q6, Q7, Q8, Q9, Q10, Q11, Q12, Q13, Q14, Q15]), "width" : 1 * mm, "tangentPropagation" : true});
        }
        {
            var Q0;
            Q0=makeQuery(id+"F1.opExtrude","CAP_EDGE",EDGE,{"disambiguationData":[OSD([sQuery(id+"F0.wireOp",EDGE,"E114.MirrorCS")])],"isStart":false});
            var Q1;
            Q1=makeQuery(id+"F1.opExtrude","CAP_EDGE",EDGE,{"disambiguationData":[OSD([sQuery(id+"F0.wireOp",EDGE,"E121.MirrorCS")])],"isStart":false});
            var Q2;
            Q2=makeQuery(id+"F1.opExtrude","CAP_EDGE",EDGE,{"disambiguationData":[OSD([sQuery(id+"F0.wireOp",EDGE,"E116.MirrorCS")])],"isStart":false});
            var Q3;
            Q3=makeQuery(id+"F1.opExtrude","CAP_EDGE",EDGE,{"disambiguationData":[OSD([sQuery(id+"F0.wireOp",EDGE,"E120.MirrorCS")])],"isStart":false});
            var Q4;
            Q4=makeQuery(id+"F1.opExtrude","CAP_EDGE",EDGE,{"disambiguationData":[OSD([sQuery(id+"F0.wireOp",EDGE,"E130.MirrorCS")])],"isStart":false});
            var Q5;
            Q5=makeQuery(id+"F1.opExtrude","CAP_EDGE",EDGE,{"disambiguationData":[OSD([sQuery(id+"F0.wireOp",EDGE,"E122.MirrorCS")])],"isStart":false});
            var Q6;
            Q6=makeQuery(id+"F1.opExtrude","CAP_EDGE",EDGE,{"disambiguationData":[OSD([sQuery(id+"F0.wireOp",EDGE,"E127.MirrorCS")])],"isStart":false});
            var Q7;
            Q7=makeQuery(id+"F1.opExtrude","CAP_EDGE",EDGE,{"disambiguationData":[OSD([sQuery(id+"F0.wireOp",EDGE,"E136.MirrorCS")])],"isStart":false});
            var Q8;
            Q8=makeQuery(id+"F1.opExtrude","CAP_EDGE",EDGE,{"disambiguationData":[OSD([sQuery(id+"F0.wireOp",EDGE,"E122.MirrorCS")])],"isStart":true});
            var Q9;
            Q9=makeQuery(id+"F1.opExtrude","CAP_EDGE",EDGE,{"disambiguationData":[OSD([sQuery(id+"F0.wireOp",EDGE,"E127.MirrorCS")])],"isStart":true});
            var Q10;
            Q10=makeQuery(id+"F1.opExtrude","CAP_EDGE",EDGE,{"disambiguationData":[OSD([sQuery(id+"F0.wireOp",EDGE,"E130.MirrorCS")])],"isStart":true});
            var Q11;
            Q11=makeQuery(id+"F1.opExtrude","CAP_EDGE",EDGE,{"disambiguationData":[OSD([sQuery(id+"F0.wireOp",EDGE,"E136.MirrorCS")])],"isStart":true});
            var Q12;
            Q12=makeQuery(id+"F1.opExtrude","CAP_EDGE",EDGE,{"disambiguationData":[OSD([sQuery(id+"F0.wireOp",EDGE,"E121.MirrorCS")])],"isStart":true});
            var Q13;
            Q13=makeQuery(id+"F1.opExtrude","CAP_EDGE",EDGE,{"disambiguationData":[OSD([sQuery(id+"F0.wireOp",EDGE,"E114.MirrorCS")])],"isStart":true});
            var Q14;
            Q14=makeQuery(id+"F1.opExtrude","CAP_EDGE",EDGE,{"disambiguationData":[OSD([sQuery(id+"F0.wireOp",EDGE,"E116.MirrorCS")])],"isStart":true});
            var Q15;
            Q15=makeQuery(id+"F1.opExtrude","CAP_EDGE",EDGE,{"disambiguationData":[OSD([sQuery(id+"F0.wireOp",EDGE,"E120.MirrorCS")])],"isStart":true});
            chamfer(context, id + "F5", {"entities" : qUnion([Q0, Q1, Q2, Q3, Q4, Q5, Q6, Q7, Q8, Q9, Q10, Q11, Q12, Q13, Q14, Q15]), "width" : 1 * mm, "tangentPropagation" : true});
        }
        {
            var Q0;
            Q0=makeQuery(id+"F1.opExtrude","CAP_EDGE",EDGE,{"disambiguationData":[OSD([sQuery(id+"F0.wireOp",EDGE,"E62.MirrorCS")])],"isStart":false});
            var Q1;
            Q1=makeQuery(id+"F1.opExtrude","CAP_EDGE",EDGE,{"disambiguationData":[OSD([sQuery(id+"F0.wireOp",EDGE,"E55.MirrorCS")])],"isStart":false});
            var Q2;
            Q2=makeQuery(id+"F1.opExtrude","CAP_EDGE",EDGE,{"disambiguationData":[OSD([sQuery(id+"F0.wireOp",EDGE,"E63.MirrorCS")])],"isStart":false});
            var Q3;
            Q3=makeQuery(id+"F1.opExtrude","CAP_EDGE",EDGE,{"disambiguationData":[OSD([sQuery(id+"F0.wireOp",EDGE,"E67.MirrorCS")])],"isStart":false});
            var Q4;
            Q4=makeQuery(id+"F1.opExtrude","CAP_EDGE",EDGE,{"disambiguationData":[OSD([sQuery(id+"F0.wireOp",EDGE,"E61.MirrorCS")])],"isStart":false});
            var Q5;
            Q5=makeQuery(id+"F1.opExtrude","CAP_EDGE",EDGE,{"disambiguationData":[OSD([sQuery(id+"F0.wireOp",EDGE,"E66.MirrorCS")])],"isStart":false});
            var Q6;
            Q6=makeQuery(id+"F1.opExtrude","CAP_EDGE",EDGE,{"disambiguationData":[OSD([sQuery(id+"F0.wireOp",EDGE,"E65.MirrorCS")])],"isStart":false});
            var Q7;
            Q7=makeQuery(id+"F1.opExtrude","CAP_EDGE",EDGE,{"disambiguationData":[OSD([sQuery(id+"F0.wireOp",EDGE,"E54.MirrorCS")])],"isStart":false});
            var Q8;
            Q8=makeQuery(id+"F1.opExtrude","CAP_EDGE",EDGE,{"disambiguationData":[OSD([sQuery(id+"F0.wireOp",EDGE,"E66.MirrorCS")])],"isStart":true});
            var Q9;
            Q9=makeQuery(id+"F1.opExtrude","CAP_EDGE",EDGE,{"disambiguationData":[OSD([sQuery(id+"F0.wireOp",EDGE,"E61.MirrorCS")])],"isStart":true});
            var Q10;
            Q10=makeQuery(id+"F1.opExtrude","CAP_EDGE",EDGE,{"disambiguationData":[OSD([sQuery(id+"F0.wireOp",EDGE,"E67.MirrorCS")])],"isStart":true});
            var Q11;
            Q11=makeQuery(id+"F1.opExtrude","CAP_EDGE",EDGE,{"disambiguationData":[OSD([sQuery(id+"F0.wireOp",EDGE,"E63.MirrorCS")])],"isStart":true});
            var Q12;
            Q12=makeQuery(id+"F1.opExtrude","CAP_EDGE",EDGE,{"disambiguationData":[OSD([sQuery(id+"F0.wireOp",EDGE,"E62.MirrorCS")])],"isStart":true});
            var Q13;
            Q13=makeQuery(id+"F1.opExtrude","CAP_EDGE",EDGE,{"disambiguationData":[OSD([sQuery(id+"F0.wireOp",EDGE,"E55.MirrorCS")])],"isStart":true});
            var Q14;
            Q14=makeQuery(id+"F1.opExtrude","CAP_EDGE",EDGE,{"disambiguationData":[OSD([sQuery(id+"F0.wireOp",EDGE,"E54.MirrorCS")])],"isStart":true});
            var Q15;
            Q15=makeQuery(id+"F1.opExtrude","CAP_EDGE",EDGE,{"disambiguationData":[OSD([sQuery(id+"F0.wireOp",EDGE,"E65.MirrorCS")])],"isStart":true});
            chamfer(context, id + "F6", {"entities" : qUnion([Q0, Q1, Q2, Q3, Q4, Q5, Q6, Q7, Q8, Q9, Q10, Q11, Q12, Q13, Q14, Q15]), "width" : 1 * mm, "tangentPropagation" : true});
        }
        {
            var Q0;
            Q0=makeQuery(id+"F1.opExtrude","CAP_EDGE",EDGE,{"disambiguationData":[OSD([sQuery(id+"F0.wireOp",EDGE,"E128.MirrorCS")])],"isStart":false});
            var Q1;
            Q1=makeQuery(id+"F1.opExtrude","CAP_EDGE",EDGE,{"disambiguationData":[OSD([sQuery(id+"F0.wireOp",EDGE,"E133.MirrorCS")])],"isStart":false});
            var Q2;
            Q2=makeQuery(id+"F1.opExtrude","CAP_EDGE",EDGE,{"disambiguationData":[OSD([sQuery(id+"F0.wireOp",EDGE,"E138.MirrorCS")])],"isStart":false});
            var Q3;
            Q3=makeQuery(id+"F1.opExtrude","CAP_EDGE",EDGE,{"disambiguationData":[OSD([sQuery(id+"F0.wireOp",EDGE,"E118.MirrorCS")])],"isStart":false});
            var Q4;
            Q4=makeQuery(id+"F1.opExtrude","CAP_EDGE",EDGE,{"disambiguationData":[OSD([sQuery(id+"F0.wireOp",EDGE,"E124.MirrorCS")])],"isStart":false});
            var Q5;
            Q5=makeQuery(id+"F1.opExtrude","CAP_EDGE",EDGE,{"disambiguationData":[OSD([sQuery(id+"F0.wireOp",EDGE,"E134.MirrorCS")])],"isStart":false});
            var Q6;
            Q6=makeQuery(id+"F1.opExtrude","CAP_EDGE",EDGE,{"disambiguationData":[OSD([sQuery(id+"F0.wireOp",EDGE,"E129.MirrorCS")])],"isStart":false});
            var Q7;
            Q7=makeQuery(id+"F1.opExtrude","CAP_EDGE",EDGE,{"disambiguationData":[OSD([sQuery(id+"F0.wireOp",EDGE,"E123.MirrorCS")])],"isStart":false});
            var Q8;
            Q8=makeQuery(id+"F1.opExtrude","CAP_EDGE",EDGE,{"disambiguationData":[OSD([sQuery(id+"F0.wireOp",EDGE,"E118.MirrorCS")])],"isStart":true});
            var Q9;
            Q9=makeQuery(id+"F1.opExtrude","CAP_EDGE",EDGE,{"disambiguationData":[OSD([sQuery(id+"F0.wireOp",EDGE,"E133.MirrorCS")])],"isStart":true});
            var Q10;
            Q10=makeQuery(id+"F1.opExtrude","CAP_EDGE",EDGE,{"disambiguationData":[OSD([sQuery(id+"F0.wireOp",EDGE,"E124.MirrorCS")])],"isStart":true});
            var Q11;
            Q11=makeQuery(id+"F1.opExtrude","CAP_EDGE",EDGE,{"disambiguationData":[OSD([sQuery(id+"F0.wireOp",EDGE,"E128.MirrorCS")])],"isStart":true});
            var Q12;
            Q12=makeQuery(id+"F1.opExtrude","CAP_EDGE",EDGE,{"disambiguationData":[OSD([sQuery(id+"F0.wireOp",EDGE,"E138.MirrorCS")])],"isStart":true});
            var Q13;
            Q13=makeQuery(id+"F1.opExtrude","CAP_EDGE",EDGE,{"disambiguationData":[OSD([sQuery(id+"F0.wireOp",EDGE,"E134.MirrorCS")])],"isStart":true});
            var Q14;
            Q14=makeQuery(id+"F1.opExtrude","CAP_EDGE",EDGE,{"disambiguationData":[OSD([sQuery(id+"F0.wireOp",EDGE,"E129.MirrorCS")])],"isStart":true});
            var Q15;
            Q15=makeQuery(id+"F1.opExtrude","CAP_EDGE",EDGE,{"disambiguationData":[OSD([sQuery(id+"F0.wireOp",EDGE,"E123.MirrorCS")])],"isStart":true});
            chamfer(context, id + "F7", {"entities" : qUnion([Q0, Q1, Q2, Q3, Q4, Q5, Q6, Q7, Q8, Q9, Q10, Q11, Q12, Q13, Q14, Q15]), "width" : 1 * mm, "tangentPropagation" : true});
        }
        {
            var Q0;
            Q0=makeQuery(id+"F1.opExtrude","CAP_EDGE",EDGE,{"disambiguationData":[OSD([sQuery(id+"F0.wireOp",EDGE,"E186.MirrorC")])],"isStart":false});
            var Q1;
            Q1=makeQuery(id+"F1.opExtrude","CAP_EDGE",EDGE,{"disambiguationData":[OSD([sQuery(id+"F0.wireOp",EDGE,"E185")])],"isStart":false});
            var Q2;
            Q2=makeQuery(id+"F1.opExtrude","CAP_EDGE",EDGE,{"disambiguationData":[OSD([sQuery(id+"F0.wireOp",EDGE,"E186.MirrorC")])],"isStart":true});
            var Q3;
            Q3=makeQuery(id+"F1.opExtrude","CAP_EDGE",EDGE,{"disambiguationData":[OSD([sQuery(id+"F0.wireOp",EDGE,"E185")])],"isStart":true});
            chamfer(context, id + "F8", {"entities" : qUnion([Q0, Q1, Q2, Q3]), "width" : 1 * mm, "tangentPropagation" : true});
        }
        {
            var Q0;
            Q0=makeQuery(id+"F1.opExtrude","CAP_EDGE",EDGE,{"disambiguationData":[OSD([sQuery(id+"F0.wireOp",EDGE,"E18")])],"isStart":false});
            var Q1;
            Q1=makeQuery(id+"F1.opExtrude","CAP_EDGE",EDGE,{"disambiguationData":[OSD([sQuery(id+"F0.wireOp",EDGE,"E19")])],"isStart":false});
            var Q2;
            Q2=makeQuery(id+"F1.opExtrude","CAP_EDGE",EDGE,{"disambiguationData":[OSD([sQuery(id+"F0.wireOp",EDGE,"E19")])],"isStart":true});
            var Q3;
            Q3=makeQuery(id+"F1.opExtrude","CAP_EDGE",EDGE,{"disambiguationData":[OSD([sQuery(id+"F0.wireOp",EDGE,"E18")])],"isStart":true});
            var Q4;
            Q4=makeQuery(id+"F1.opExtrude","CAP_EDGE",EDGE,{"disambiguationData":[OSD([sQuery(id+"F0.wireOp",EDGE,"E21"),sQuery(id+"F0.wireOp",EDGE,"E78.MirrorCS")])],"isStart":true});
            var Q5;
            Q5=makeQuery(id+"F1.opExtrude","CAP_EDGE",EDGE,{"disambiguationData":[OSD([sQuery(id+"F0.wireOp",EDGE,"E21"),sQuery(id+"F0.wireOp",EDGE,"E78.MirrorCS")])],"isStart":false});
            var Q6;
            Q6=makeQuery(id+"F1.opExtrude","CAP_EDGE",EDGE,{"disambiguationData":[OSD([sQuery(id+"F0.wireOp",EDGE,"E85.MirrorCS")])],"isStart":true});
            var Q7;
            Q7=makeQuery(id+"F1.opExtrude","CAP_EDGE",EDGE,{"disambiguationData":[OSD([sQuery(id+"F0.wireOp",EDGE,"E85.MirrorCS")])],"isStart":false});
            var Q8;
            Q8=makeQuery(id+"F1.opExtrude","CAP_EDGE",EDGE,{"disambiguationData":[OSD([sQuery(id+"F0.wireOp",EDGE,"E70.MirrorCS")])],"isStart":false});
            var Q9;
            Q9=makeQuery(id+"F1.opExtrude","CAP_EDGE",EDGE,{"disambiguationData":[OSD([sQuery(id+"F0.wireOp",EDGE,"E70.MirrorCS")])],"isStart":true});
            var Q10;
            Q10=makeQuery(id+"F1.opExtrude","CAP_EDGE",EDGE,{"disambiguationData":[OSD([sQuery(id+"F0.wireOp",EDGE,"E191.MirrorCS")])],"isStart":true});
            var Q11;
            Q11=makeQuery(id+"F1.opExtrude","CAP_EDGE",EDGE,{"disambiguationData":[OSD([sQuery(id+"F0.wireOp",EDGE,"E191.MirrorCS")])],"isStart":false});
            var Q12;
            Q12=makeQuery(id+"F1.opExtrude","CAP_EDGE",EDGE,{"disambiguationData":[OSD([sQuery(id+"F0.wireOp",EDGE,"E196.MirrorCS")])],"isStart":false});
            var Q13;
            Q13=makeQuery(id+"F1.opExtrude","CAP_EDGE",EDGE,{"disambiguationData":[OSD([sQuery(id+"F0.wireOp",EDGE,"E196.MirrorCS")])],"isStart":true});
            var Q14;
            Q14=makeQuery(id+"F1.opExtrude","CAP_EDGE",EDGE,{"disambiguationData":[OSD([sQuery(id+"F0.wireOp",EDGE,"E192.MirrorCS"),sQuery(id+"F0.wireOp",EDGE,"E195.MirrorCS")])],"isStart":false});
            var Q15;
            Q15=makeQuery(id+"F1.opExtrude","CAP_EDGE",EDGE,{"disambiguationData":[OSD([sQuery(id+"F0.wireOp",EDGE,"E192.MirrorCS"),sQuery(id+"F0.wireOp",EDGE,"E195.MirrorCS")])],"isStart":true});
            var Q16;
            Q16=makeQuery(id+"F1.opExtrude","CAP_EDGE",EDGE,{"disambiguationData":[OSD([sQuery(id+"F0.wireOp",EDGE,"E194.MirrorCS")])],"isStart":false});
            var Q17;
            Q17=makeQuery(id+"F1.opExtrude","CAP_EDGE",EDGE,{"disambiguationData":[OSD([sQuery(id+"F0.wireOp",EDGE,"E194.MirrorCS")])],"isStart":true});
            var Q18;
            Q18=makeQuery(id+"F1.opExtrude","CAP_EDGE",EDGE,{"disambiguationData":[OSD([sQuery(id+"F0.wireOp",EDGE,"E193.MirrorCS")])],"isStart":true});
            var Q19;
            Q19=makeQuery(id+"F1.opExtrude","CAP_EDGE",EDGE,{"disambiguationData":[OSD([sQuery(id+"F0.wireOp",EDGE,"E193.MirrorCS")])],"isStart":false});
            var Q20;
            Q20=makeQuery(id+"F1.opExtrude","CAP_EDGE",EDGE,{"disambiguationData":[OSD([sQuery(id+"F0.wireOp",EDGE,"E153.MirrorCS")])],"isStart":false});
            var Q21;
            Q21=makeQuery(id+"F1.opExtrude","CAP_EDGE",EDGE,{"disambiguationData":[OSD([sQuery(id+"F0.wireOp",EDGE,"E153.MirrorCS")])],"isStart":true});
            var Q22;
            Q22=makeQuery(id+"F1.opExtrude","CAP_EDGE",EDGE,{"disambiguationData":[OSD([sQuery(id+"F0.wireOp",EDGE,"E184.MirrorCS")])],"isStart":false});
            var Q23;
            Q23=makeQuery(id+"F1.opExtrude","CAP_EDGE",EDGE,{"disambiguationData":[OSD([sQuery(id+"F0.wireOp",EDGE,"E184.MirrorCS")])],"isStart":true});
            var Q24;
            Q24=makeQuery(id+"F1.opExtrude","CAP_EDGE",EDGE,{"disambiguationData":[OSD([sQuery(id+"F0.wireOp",EDGE,"E148.MirrorCS"),sQuery(id+"F0.wireOp",EDGE,"E155.MirrorCS")])],"isStart":false});
            var Q25;
            Q25=makeQuery(id+"F1.opExtrude","CAP_EDGE",EDGE,{"disambiguationData":[OSD([sQuery(id+"F0.wireOp",EDGE,"E148.MirrorCS"),sQuery(id+"F0.wireOp",EDGE,"E155.MirrorCS")])],"isStart":true});
            var Q26;
            Q26=makeQuery(id+"F1.opExtrude","CAP_EDGE",EDGE,{"disambiguationData":[OSD([sQuery(id+"F0.wireOp",EDGE,"E154.MirrorCS")])],"isStart":false});
            var Q27;
            Q27=makeQuery(id+"F1.opExtrude","CAP_EDGE",EDGE,{"disambiguationData":[OSD([sQuery(id+"F0.wireOp",EDGE,"E154.MirrorCS")])],"isStart":true});
            var Q28;
            Q28=makeQuery(id+"F1.opExtrude","CAP_EDGE",EDGE,{"disambiguationData":[OSD([sQuery(id+"F0.wireOp",EDGE,"E183.MirrorCS")])],"isStart":true});
            var Q29;
            Q29=makeQuery(id+"F1.opExtrude","CAP_EDGE",EDGE,{"disambiguationData":[OSD([sQuery(id+"F0.wireOp",EDGE,"E183.MirrorCS")])],"isStart":false});
            var Q30;
            Q30=makeQuery(id+"F1.opExtrude","CAP_EDGE",EDGE,{"disambiguationData":[OSD([sQuery(id+"F0.wireOp",EDGE,"E173.MirrorCS")])],"isStart":false});
            var Q31;
            Q31=makeQuery(id+"F1.opExtrude","CAP_EDGE",EDGE,{"disambiguationData":[OSD([sQuery(id+"F0.wireOp",EDGE,"E173.MirrorCS")])],"isStart":true});
            var Q32;
            Q32=makeQuery(id+"F1.opExtrude","CAP_EDGE",EDGE,{"disambiguationData":[OSD([sQuery(id+"F0.wireOp",EDGE,"E187")])],"isStart":true});
            var Q33;
            Q33=makeQuery(id+"F1.opExtrude","CAP_EDGE",EDGE,{"disambiguationData":[OSD([sQuery(id+"F0.wireOp",EDGE,"E187")])],"isStart":false});
            var Q34;
            Q34=makeQuery(id+"F1.opExtrude","CAP_EDGE",EDGE,{"disambiguationData":[OSD([sQuery(id+"F0.wireOp",EDGE,"E188"),sQuery(id+"F0.wireOp",EDGE,"E190.MirrorCS")])],"isStart":true});
            var Q35;
            Q35=makeQuery(id+"F1.opExtrude","CAP_EDGE",EDGE,{"disambiguationData":[OSD([sQuery(id+"F0.wireOp",EDGE,"E188"),sQuery(id+"F0.wireOp",EDGE,"E190.MirrorCS")])],"isStart":false});
            var Q36;
            Q36=makeQuery(id+"F1.opExtrude","CAP_EDGE",EDGE,{"disambiguationData":[OSD([sQuery(id+"F0.wireOp",EDGE,"E189.MirrorCS")])],"isStart":true});
            var Q37;
            Q37=makeQuery(id+"F1.opExtrude","CAP_EDGE",EDGE,{"disambiguationData":[OSD([sQuery(id+"F0.wireOp",EDGE,"E189.MirrorCS")])],"isStart":false});
            var Q38;
            Q38=makeQuery(id+"F1.opExtrude","CAP_EDGE",EDGE,{"disambiguationData":[OSD([sQuery(id+"F0.wireOp",EDGE,"E20")])],"isStart":true});
            var Q39;
            Q39=makeQuery(id+"F1.opExtrude","CAP_EDGE",EDGE,{"disambiguationData":[OSD([sQuery(id+"F0.wireOp",EDGE,"E20")])],"isStart":false});
            chamfer(context, id + "F9", {"entities" : qUnion([Q0, Q1, Q2, Q3, Q4, Q5, Q6, Q7, Q8, Q9, Q10, Q11, Q12, Q13, Q14, Q15, Q16, Q17, Q18, Q19, Q20, Q21, Q22, Q23, Q24, Q25, Q26, Q27, Q28, Q29, Q30, Q31, Q32, Q33, Q34, Q35, Q36, Q37, Q38, Q39]), "width" : 1 * mm, "tangentPropagation" : true});
        }
        {
            var Q0;
            Q0=makeQuery(id+"F1.opExtrude","CAP_EDGE",EDGE,{"disambiguationData":[OSD([sQuery(id+"F0.wireOp",EDGE,"E197.2")])],"isStart":true});
            var Q1;
            Q1=makeQuery(id+"F1.opExtrude","CAP_EDGE",EDGE,{"disambiguationData":[OSD([sQuery(id+"F0.wireOp",EDGE,"E197.2")])],"isStart":false});
            var Q2;
            Q2=makeQuery(id+"F1.opExtrude","CAP_EDGE",EDGE,{"disambiguationData":[OSD([sQuery(id+"F0.wireOp",EDGE,"E197.3")])],"isStart":true});
            var Q3;
            Q3=makeQuery(id+"F1.opExtrude","CAP_EDGE",EDGE,{"disambiguationData":[OSD([sQuery(id+"F0.wireOp",EDGE,"E197.3")])],"isStart":false});
            var Q4;
            Q4=makeQuery(id+"F1.opExtrude","CAP_EDGE",EDGE,{"disambiguationData":[OSD([sQuery(id+"F0.wireOp",EDGE,"E197.4")])],"isStart":false});
            var Q5;
            Q5=makeQuery(id+"F1.opExtrude","CAP_EDGE",EDGE,{"disambiguationData":[OSD([sQuery(id+"F0.wireOp",EDGE,"E197.4")])],"isStart":true});
            var Q6;
            Q6=makeQuery(id+"F1.opExtrude","CAP_EDGE",EDGE,{"disambiguationData":[OSD([sQuery(id+"F0.wireOp",EDGE,"E197.5")])],"isStart":false});
            var Q7;
            Q7=makeQuery(id+"F1.opExtrude","CAP_EDGE",EDGE,{"disambiguationData":[OSD([sQuery(id+"F0.wireOp",EDGE,"E197.5")])],"isStart":true});
            var Q8;
            Q8=makeQuery(id+"F1.opExtrude","CAP_EDGE",EDGE,{"disambiguationData":[OSD([sQuery(id+"F0.wireOp",EDGE,"E197.0")])],"isStart":false});
            var Q9;
            Q9=makeQuery(id+"F1.opExtrude","CAP_EDGE",EDGE,{"disambiguationData":[OSD([sQuery(id+"F0.wireOp",EDGE,"E197.0")])],"isStart":true});
            var Q10;
            Q10=makeQuery(id+"F1.opExtrude","CAP_EDGE",EDGE,{"disambiguationData":[OSD([sQuery(id+"F0.wireOp",EDGE,"E201.MirrorCS")])],"isStart":false});
            var Q11;
            Q11=makeQuery(id+"F1.opExtrude","CAP_EDGE",EDGE,{"disambiguationData":[OSD([sQuery(id+"F0.wireOp",EDGE,"E201.MirrorCS")])],"isStart":true});
            var Q12;
            Q12=makeQuery(id+"F1.opExtrude","CAP_EDGE",EDGE,{"disambiguationData":[OSD([sQuery(id+"F0.wireOp",EDGE,"E202.MirrorCS")])],"isStart":false});
            var Q13;
            Q13=makeQuery(id+"F1.opExtrude","CAP_EDGE",EDGE,{"disambiguationData":[OSD([sQuery(id+"F0.wireOp",EDGE,"E202.MirrorCS")])],"isStart":true});
            var Q14;
            Q14=makeQuery(id+"F1.opExtrude","CAP_EDGE",EDGE,{"disambiguationData":[OSD([sQuery(id+"F0.wireOp",EDGE,"E200.MirrorCS")])],"isStart":true});
            var Q15;
            Q15=makeQuery(id+"F1.opExtrude","CAP_EDGE",EDGE,{"disambiguationData":[OSD([sQuery(id+"F0.wireOp",EDGE,"E200.MirrorCS")])],"isStart":false});
            var Q16;
            Q16=makeQuery(id+"F1.opExtrude","CAP_EDGE",EDGE,{"disambiguationData":[OSD([sQuery(id+"F0.wireOp",EDGE,"E199.MirrorCS")])],"isStart":true});
            var Q17;
            Q17=makeQuery(id+"F1.opExtrude","CAP_EDGE",EDGE,{"disambiguationData":[OSD([sQuery(id+"F0.wireOp",EDGE,"E199.MirrorCS")])],"isStart":false});
            var Q18;
            Q18=makeQuery(id+"F1.opExtrude","CAP_EDGE",EDGE,{"disambiguationData":[OSD([sQuery(id+"F0.wireOp",EDGE,"E198.MirrorCS")])],"isStart":true});
            var Q19;
            Q19=makeQuery(id+"F1.opExtrude","CAP_EDGE",EDGE,{"disambiguationData":[OSD([sQuery(id+"F0.wireOp",EDGE,"E198.MirrorCS")])],"isStart":false});
            var Q20;
            Q20=makeQuery(id+"F1.opExtrude","CAP_EDGE",EDGE,{"disambiguationData":[OSD([sQuery(id+"F0.wireOp",EDGE,"E204.MirrorCS")])],"isStart":false});
            var Q21;
            Q21=makeQuery(id+"F1.opExtrude","CAP_EDGE",EDGE,{"disambiguationData":[OSD([sQuery(id+"F0.wireOp",EDGE,"E204.MirrorCS")])],"isStart":true});
            var Q22;
            Q22=makeQuery(id+"F1.opExtrude","CAP_EDGE",EDGE,{"disambiguationData":[OSD([sQuery(id+"F0.wireOp",EDGE,"E205.MirrorCS")])],"isStart":false});
            var Q23;
            Q23=makeQuery(id+"F1.opExtrude","CAP_EDGE",EDGE,{"disambiguationData":[OSD([sQuery(id+"F0.wireOp",EDGE,"E205.MirrorCS")])],"isStart":true});
            var Q24;
            Q24=makeQuery(id+"F1.opExtrude","CAP_EDGE",EDGE,{"disambiguationData":[OSD([sQuery(id+"F0.wireOp",EDGE,"E207.MirrorCS")])],"isStart":false});
            var Q25;
            Q25=makeQuery(id+"F1.opExtrude","CAP_EDGE",EDGE,{"disambiguationData":[OSD([sQuery(id+"F0.wireOp",EDGE,"E207.MirrorCS")])],"isStart":true});
            var Q26;
            Q26=makeQuery(id+"F1.opExtrude","CAP_EDGE",EDGE,{"disambiguationData":[OSD([sQuery(id+"F0.wireOp",EDGE,"E203.MirrorCS")])],"isStart":false});
            var Q27;
            Q27=makeQuery(id+"F1.opExtrude","CAP_EDGE",EDGE,{"disambiguationData":[OSD([sQuery(id+"F0.wireOp",EDGE,"E203.MirrorCS")])],"isStart":true});
            var Q28;
            Q28=makeQuery(id+"F1.opExtrude","CAP_EDGE",EDGE,{"disambiguationData":[OSD([sQuery(id+"F0.wireOp",EDGE,"E206.MirrorCS")])],"isStart":false});
            var Q29;
            Q29=makeQuery(id+"F1.opExtrude","CAP_EDGE",EDGE,{"disambiguationData":[OSD([sQuery(id+"F0.wireOp",EDGE,"E206.MirrorCS")])],"isStart":true});
            var Q30;
            Q30=makeQuery(id+"F1.opExtrude","CAP_EDGE",EDGE,{"disambiguationData":[OSD([sQuery(id+"F0.wireOp",EDGE,"E210.MirrorCS")])],"isStart":false});
            var Q31;
            Q31=makeQuery(id+"F1.opExtrude","CAP_EDGE",EDGE,{"disambiguationData":[OSD([sQuery(id+"F0.wireOp",EDGE,"E210.MirrorCS")])],"isStart":true});
            var Q32;
            Q32=makeQuery(id+"F1.opExtrude","CAP_EDGE",EDGE,{"disambiguationData":[OSD([sQuery(id+"F0.wireOp",EDGE,"E209.MirrorCS")])],"isStart":false});
            var Q33;
            Q33=makeQuery(id+"F1.opExtrude","CAP_EDGE",EDGE,{"disambiguationData":[OSD([sQuery(id+"F0.wireOp",EDGE,"E209.MirrorCS")])],"isStart":true});
            var Q34;
            Q34=makeQuery(id+"F1.opExtrude","CAP_EDGE",EDGE,{"disambiguationData":[OSD([sQuery(id+"F0.wireOp",EDGE,"E212.MirrorCS")])],"isStart":true});
            var Q35;
            Q35=makeQuery(id+"F1.opExtrude","CAP_EDGE",EDGE,{"disambiguationData":[OSD([sQuery(id+"F0.wireOp",EDGE,"E212.MirrorCS")])],"isStart":false});
            var Q36;
            Q36=makeQuery(id+"F1.opExtrude","CAP_EDGE",EDGE,{"disambiguationData":[OSD([sQuery(id+"F0.wireOp",EDGE,"E211.MirrorCS")])],"isStart":false});
            var Q37;
            Q37=makeQuery(id+"F1.opExtrude","CAP_EDGE",EDGE,{"disambiguationData":[OSD([sQuery(id+"F0.wireOp",EDGE,"E211.MirrorCS")])],"isStart":true});
            var Q38;
            Q38=makeQuery(id+"F1.opExtrude","CAP_EDGE",EDGE,{"disambiguationData":[OSD([sQuery(id+"F0.wireOp",EDGE,"E208.MirrorCS")])],"isStart":false});
            var Q39;
            Q39=makeQuery(id+"F1.opExtrude","CAP_EDGE",EDGE,{"disambiguationData":[OSD([sQuery(id+"F0.wireOp",EDGE,"E208.MirrorCS")])],"isStart":true});
            chamfer(context, id + "F10", {"entities" : qUnion([Q0, Q1, Q2, Q3, Q4, Q5, Q6, Q7, Q8, Q9, Q10, Q11, Q12, Q13, Q14, Q15, Q16, Q17, Q18, Q19, Q20, Q21, Q22, Q23, Q24, Q25, Q26, Q27, Q28, Q29, Q30, Q31, Q32, Q33, Q34, Q35, Q36, Q37, Q38, Q39]), "width" : 1 * mm, "tangentPropagation" : true});
        }
    });
